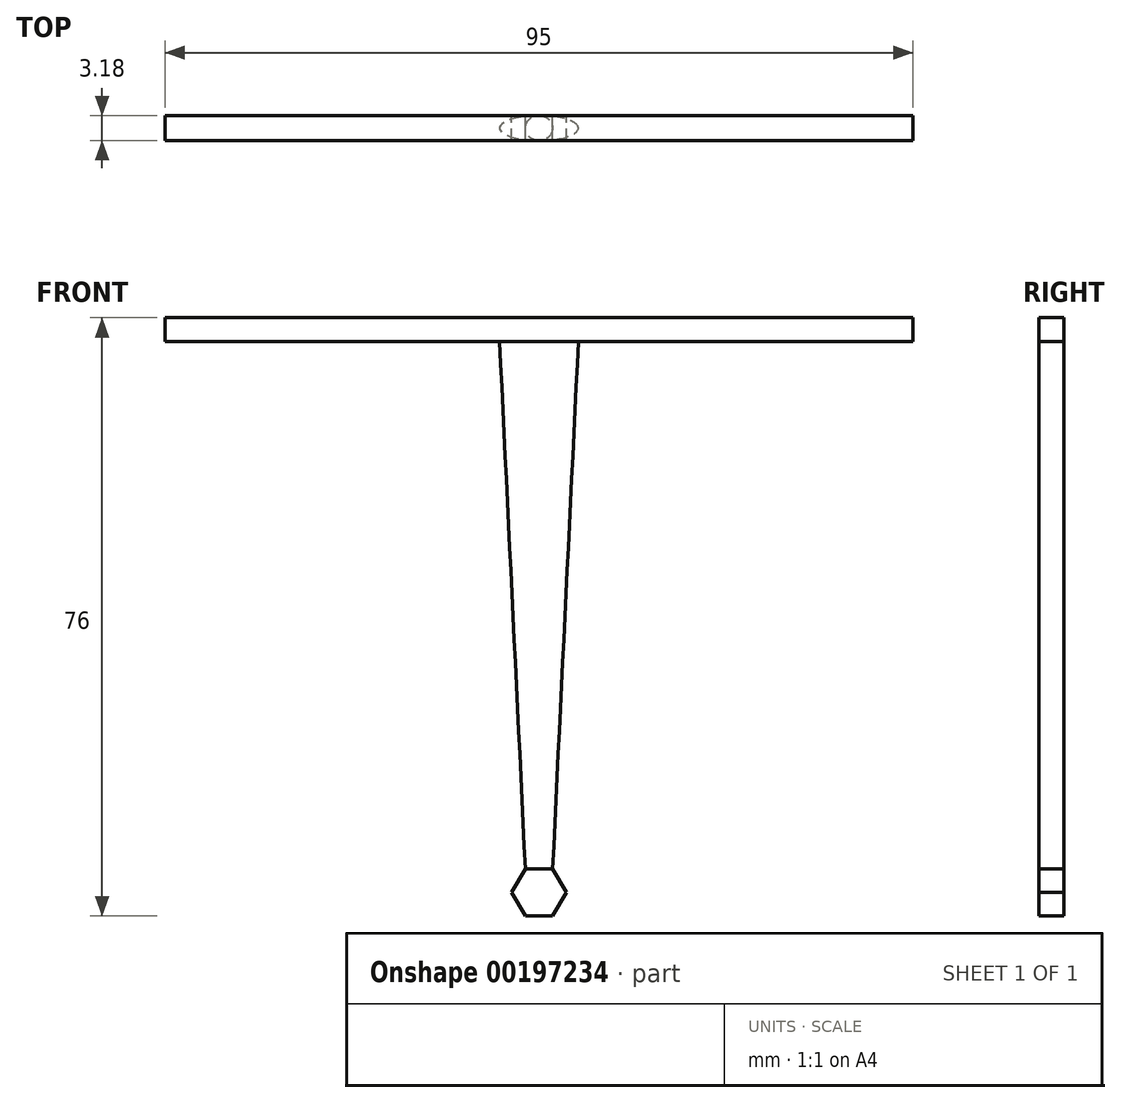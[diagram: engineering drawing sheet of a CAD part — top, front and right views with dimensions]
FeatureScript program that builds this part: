
annotation { "Feature Type Name" : "Feature", "Feature Type Description" : "" }
export const myFeature = defineFeature(function(context is Context, id is Id, definition is map)
    precondition{}
    {
        {
            var Q0;
            Q0=qCreatedBy(makeId("Front.planeOp"),FACE);
            var sketch = newSketch(context, id + "F0", { "sketchPlane" : qUnion([Q0])});
            skLineSegment(sketch, "E0.bottom", {"start": v(-47.5, 3) * mm, "end": v(47.5, 3) * mm});
            skLineSegment(sketch, "E0.top", {"start": v(-47.5, 0) * mm, "end": v(47.5, 0) * mm});
            skLineSegment(sketch, "E0.left", {"start": v(-47.5, 3) * mm, "end": v(-47.5, 0) * mm});
            skLineSegment(sketch, "E0.right", {"start": v(47.5, 3) * mm, "end": v(47.5, 0) * mm});
            skSolve(sketch);
        }
        {
            var Q0;
            Q0=makeQuery(id+"F0.imprint","IMPRINT",FACE,{"disambiguationData":[TD([[makeQuery(id+"F0.imprint","IMPRINT",EDGE,{"derivedFrom":sQuery(id+"F0.wireOp",EDGE,"E0.top")}),1.0]])]});
            var Q1;
            {var subQ0=sQuery(id+"F0.wireOp",EDGE,"e0781c13-b5c1-46e0-a9c2-7ad328b582f5.sketch_text.stroke-2");var subQ1=sQuery(id+"F0.wireOp",EDGE,"E0.bottom");var subQ2=makeQuery(id+"F0.imprint","INTERSECT",VERTEX,{"derivedFrom":[subQ1,subQ0]});Q1=makeQuery(id+"F0.imprint","IMPRINT",FACE,{"disambiguationData":[TD([[makeQuery(id+"F0.imprint","IMPRINT",EDGE,{"disambiguationData":[TD([[subQ2,-1.0]])],"derivedFrom":subQ1}),-1.0]])]});}
            var Q2;
            {var subQ0=sQuery(id+"F0.wireOp",EDGE,"e0781c13-b5c1-46e0-a9c2-7ad328b582f5.sketch_text.stroke-32");var subQ1=sQuery(id+"F0.wireOp",EDGE,"E0.bottom");var subQ2=makeQuery(id+"F0.imprint","INTERSECT",VERTEX,{"derivedFrom":[subQ1,subQ0]});Q2=makeQuery(id+"F0.imprint","IMPRINT",FACE,{"disambiguationData":[TD([[makeQuery(id+"F0.imprint","IMPRINT",EDGE,{"disambiguationData":[TD([[subQ2,-1.0]])],"derivedFrom":subQ1}),-1.0]])]});}
            var Q3;
            {var subQ5=sQuery(id+"F0.wireOp",EDGE,"e0781c13-b5c1-46e0-a9c2-7ad328b582f5.sketch_text.stroke-46");Q3=makeQuery(id+"F0.imprint","IMPRINT",FACE,{"disambiguationData":[TD([[makeQuery(id+"F0.imprint","IMPRINT",EDGE,{"derivedFrom":subQ5}),-1.0]])]});}
            extrude(context, id + "F1", {"entities" : qUnion([Q0, Q1, Q2, Q3]), "depth" : 3.17 * mm});
        }
        {
            var Q0;
            Q0=qCreatedBy(makeId("Top.planeOp"),FACE);
            var sketch = newSketch(context, id + "F2", { "sketchPlane" : qUnion([Q0])});
            skLineSegment(sketch, "E1.bottom", {"start": v(0, 0) * mm, "end": v(2.5, 0) * mm, "construction": true});
            skLineSegment(sketch, "E1.top", {"start": v(0, -3.17) * mm, "end": v(2.5, -3.17) * mm, "construction": true});
            skLineSegment(sketch, "E1.left", {"start": v(0, 0) * mm, "end": v(0, -3.18) * mm, "construction": true});
            skLineSegment(sketch, "E1.right", {"start": v(2.5, 0) * mm, "end": v(2.5, -3.17) * mm, "construction": true});
            skEllipse(sketch, "E2", {"center": v(0, -1.59) * mm, "majorRadius": 5 * mm, "minorRadius": 1.59 * mm, "majorAxis": v(1, 0)});
            skSolve(sketch);
        }
        {
            var Q0;
            Q0=qCreatedBy(makeId("Top.planeOp"),FACE);
            cPlane(context, id + "F3", {"entities" : qUnion([Q0]), "cplaneType" : CPlaneType.OFFSET, "offset" : 70 * mm, "oppositeDirection" : true, "width" : 150 * mm, "height" : 150 * mm});
        }
        {
            var Q0;
            Q0=qCreatedBy(id+"F3.planeOp",FACE);
            var sketch = newSketch(context, id + "F4", { "sketchPlane" : qUnion([Q0])});
            skPoint(sketch, "E3", {"position": v(0, 0) * mm});
            skLineSegment(sketch, "E4.0", {"start": v(-50.9, -1.59) * mm, "end": v(49.1, -1.59) * mm, "construction": true});
            skLineSegment(sketch, "E5.0", {"start": v(0, 0) * mm, "end": v(0, -3.17) * mm, "construction": true});
            skCircle(sketch, "E6", {"center": v(0, -1.59) * mm, "radius": 1.59 * mm});
            skSolve(sketch);
        }
        {
            var Q1;
            Q1=makeQuery(id+"F2.imprint","IMPRINT",FACE,{"disambiguationData":[TD([[makeQuery(id+"F2.imprint","IMPRINT",EDGE,{"derivedFrom":sQuery(id+"F2.wireOp",EDGE,"E2")}),1.0]])]});
            var Q2;
            Q2=makeQuery(id+"F4.imprint","IMPRINT",FACE,{"disambiguationData":[TD([[makeQuery(id+"F4.imprint","IMPRINT",EDGE,{"derivedFrom":sQuery(id+"F4.wireOp",EDGE,"E6")}),1.0]])]});
            loft(context, id + "F5", {"operationType" : NewBodyOperationType.ADD, "sheetProfilesArray" : [{ "sheetProfileEntities" : qUnion([Q1]) }, { "sheetProfileEntities" : qUnion([Q2]) }]});
        }
        {
            var Q0;
            Q0=qCreatedBy(makeId("Front.planeOp"),FACE);
            var sketch = newSketch(context, id + "F6", { "sketchPlane" : qUnion([Q0])});
            skLineSegment(sketch, "E7.bottom", {"start": v(3, -73) * mm, "end": v(-3, -73) * mm, "construction": true});
            skLineSegment(sketch, "E7.top", {"start": v(3, -67) * mm, "end": v(-3, -67) * mm, "construction": true});
            skLineSegment(sketch, "E7.left", {"start": v(3, -73) * mm, "end": v(3, -67) * mm, "construction": true});
            skLineSegment(sketch, "E7.right", {"start": v(-3, -73) * mm, "end": v(-3, -67) * mm, "construction": true});
            skPoint(sketch, "E7.middle", {"position": v(0, -70) * mm});
            skCircle(sketch, "E8.cCircle", {"center": v(0, -70) * mm, "radius": 3 * mm, "construction": true});
            skLineSegment(sketch, "E8.0", {"start": v(0, -73) * mm, "end": v(-2.6, -71.5) * mm, "construction": true});
            skLineSegment(sketch, "E8.1", {"start": v(-2.6, -71.5) * mm, "end": v(-2.6, -68.5) * mm, "construction": true});
            skLineSegment(sketch, "E8.2", {"start": v(-2.6, -68.5) * mm, "end": v(0, -67) * mm, "construction": true});
            skLineSegment(sketch, "E8.3", {"start": v(0, -67) * mm, "end": v(2.6, -68.5) * mm, "construction": true});
            skLineSegment(sketch, "E8.4", {"start": v(2.6, -68.5) * mm, "end": v(2.6, -71.5) * mm, "construction": true});
            skLineSegment(sketch, "E8.5", {"start": v(2.6, -71.5) * mm, "end": v(0, -73) * mm, "construction": true});
            skLineSegment(sketch, "E9.0", {"start": v(1.73, -73) * mm, "end": v(-1.73, -73) * mm});
            skLineSegment(sketch, "E9.1", {"start": v(-1.73, -73) * mm, "end": v(-3.46, -70) * mm});
            skLineSegment(sketch, "E9.2", {"start": v(-3.46, -70) * mm, "end": v(-1.73, -67) * mm});
            skLineSegment(sketch, "E9.3", {"start": v(-1.73, -67) * mm, "end": v(1.73, -67) * mm});
            skLineSegment(sketch, "E9.4", {"start": v(1.73, -67) * mm, "end": v(3.46, -70) * mm});
            skLineSegment(sketch, "E9.5", {"start": v(3.46, -70) * mm, "end": v(1.73, -73) * mm});
            skPoint(sketch, "E9.0.midPoint", {"position": v(0, -73) * mm});
            skSolve(sketch);
        }
        {
            var Q0;
            Q0=makeQuery(id+"F6.imprint","IMPRINT",FACE,{"disambiguationData":[TD([[makeQuery(id+"F6.imprint","IMPRINT",EDGE,{"derivedFrom":sQuery(id+"F6.wireOp",EDGE,"E9.0")}),-1.0]])]});
            extrude(context, id + "F7", {"entities" : qUnion([Q0]), "operationType" : NewBodyOperationType.ADD, "depth" : 3.17 * mm});
        }
    });
